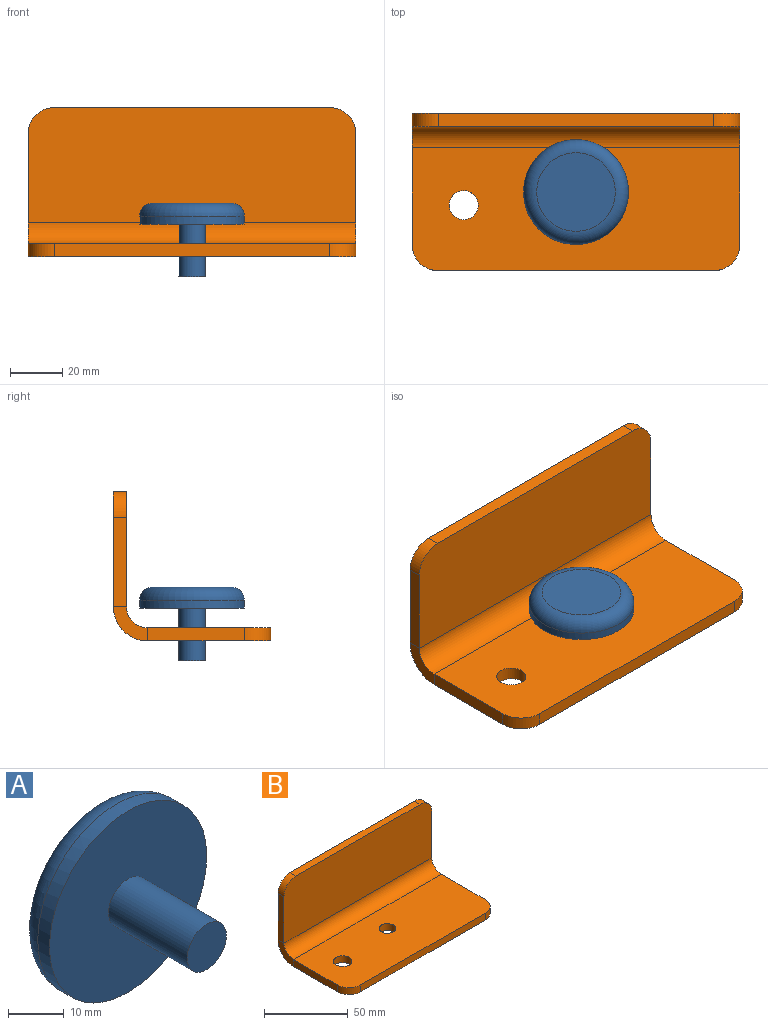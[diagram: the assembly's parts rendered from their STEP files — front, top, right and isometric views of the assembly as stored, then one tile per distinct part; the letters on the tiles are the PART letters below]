
ASSEMBLY  parts=2 mates=1
PART A: 6 faces, bbox 43.3x28x43.3 mm
  f0: plane 10x10mm, normal (0,-1,0), area 78.5mm2, adj f1
  f1: cylinder r=5mm len=20mm, axis (0,1,0), area 628.3mm2, adj f0,f2
  f2: plane 40x40mm, normal (0,-1,0), area 1178.1mm2, adj f1,f3
  f3: cylinder r=20mm len=40mm, axis (0,1,0), area 377mm2, adj f2,f5
  f4: plane 30x30mm, normal (0,1,0), area 706.9mm2, adj f5
  f5: torus R=15mm, axis (0,1,0), area 897.3mm2, adj f3,f4
PART B: 20 faces, bbox 125x60x57 mm
  f0: plane 37x5mm, normal (-1,0,0), area 185mm2, adj f1,f2,f7,f16
  f1: plane 125x47mm, normal (0,0,-1), area 5657mm2, adj f0,f3,f4,f5,f8,f15,f16,f19
  f2: plane 125x47mm, normal (0,0,1), area 5657mm2, adj f0,f3,f4,f5,f9,f15,f16,f19
  f3: plane 37x5mm, normal (1,0,0), area 185mm2, adj f1,f2,f6,f19
  f4: plane 105x5mm, normal (0,-1,0), area 525mm2, adj f1,f2,f16,f19
  f5: cylinder r=5mm len=10mm, axis (0,0,1), area 157.1mm2, adj f1,f2
  f6: plane 13x13mm, normal (1,0,0), area 82.5mm2, adj f3,f8,f9,f10
  f7: plane 13x13mm, normal (-1,0,0), area 82.5mm2, adj f0,f8,f9,f11
  f8: cylinder r=13mm len=125mm, axis (-1,0,0), area 2552.5mm2, adj f1,f6,f7,f12
  f9: cylinder r=8mm len=125mm, axis (-1,0,0), area 1570.8mm2, adj f2,f6,f7,f13
  f10: plane 34x5mm, normal (1,0,0), area 170mm2, adj f6,f12,f13,f18
  f11: plane 34x5mm, normal (-1,0,0), area 170mm2, adj f7,f12,f13,f17
  f12: plane 125x44mm, normal (0,1,0), area 5457.1mm2, adj f8,f10,f11,f14,f17,f18
  f13: plane 125x44mm, normal (0,-1,0), area 5457.1mm2, adj f9,f10,f11,f14,f17,f18
  f14: plane 105x5mm, normal (0,0,1), area 525mm2, adj f12,f13,f17,f18
  f15: cylinder r=5.54mm len=11.09mm, axis (0,0,1), area 174.1mm2, adj f1,f2
  f16: cylinder r=10mm len=10mm, axis (0,0,1), area 78.5mm2, adj f0,f1,f2,f4
  f17: cylinder r=10mm len=10mm, axis (0,-1,0), area 78.5mm2, adj f11,f12,f13,f14
  f18: cylinder r=10mm len=10mm, axis (0,-1,0), area 78.5mm2, adj f10,f12,f13,f14
  f19: cylinder r=10mm len=10mm, axis (0,0,1), area 78.5mm2, adj f1,f2,f3,f4
PLACE A rot(axis=(0,0.71,0.71),180deg) t=(-45.25,-18.03,-25.97)mm
PLACE B t=(-45.25,-18.03,-13.47)mm
MATE fastened A.f1 <-> B.f5  axis (0,0,1) through (-45.25,-18.03,-15.97)mm
